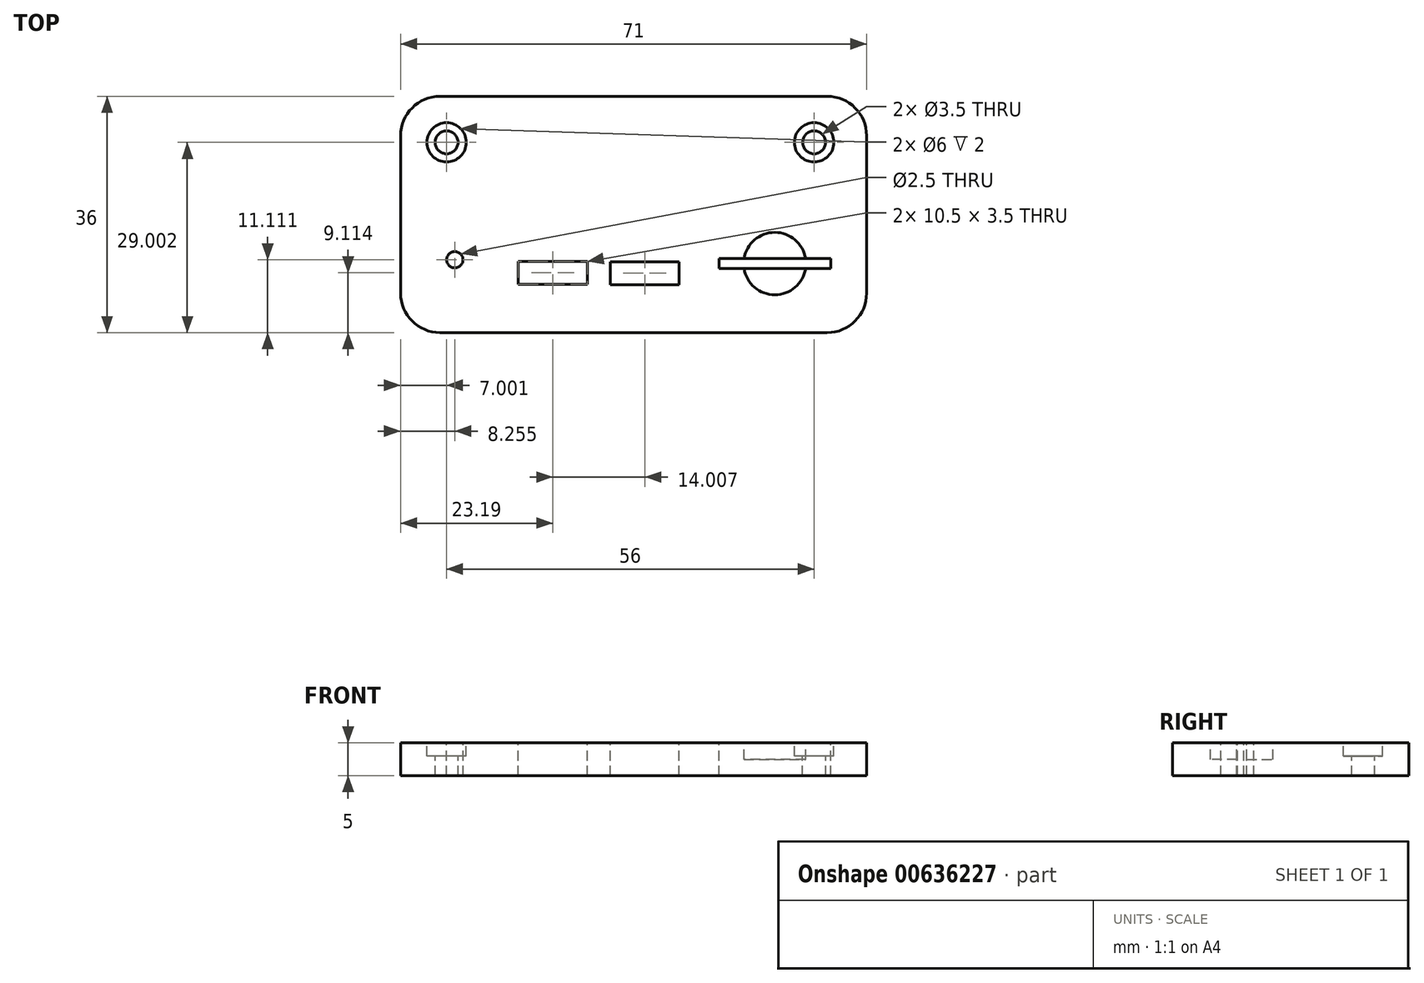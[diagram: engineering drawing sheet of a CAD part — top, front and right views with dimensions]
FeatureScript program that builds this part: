
annotation { "Feature Type Name" : "Feature", "Feature Type Description" : "" }
export const myFeature = defineFeature(function(context is Context, id is Id, definition is map)
    precondition{}
    {
        {
            var Q0;
            Q0=qCreatedBy(makeId("Top.planeOp"),FACE);
            var sketch = newSketch(context, id + "F0", { "sketchPlane" : qUnion([Q0])});
            skCircle(sketch, "E0", {"center": v(27.33, 10.52) * mm, "radius": 1.75 * mm});
            skCircle(sketch, "E1", {"center": v(-28.67, 10.52) * mm, "radius": 1.75 * mm});
            skLineSegment(sketch, "E2", {"start": v(-29.67, 17.52) * mm, "end": v(29.33, 17.52) * mm});
            skArc(sketch, "E3", {"start": v(-29.67, 17.52) * mm, "mid": v(-33.91, 15.77) * mm, "end": v(-35.67, 11.52) * mm});
            skArc(sketch, "E4", {"start": v(35.33, 11.52) * mm, "mid": v(33.57, 15.77) * mm, "end": v(29.33, 17.52) * mm});
            skLineSegment(sketch, "E5", {"start": v(-35.67, 11.52) * mm, "end": v(-35.67, -12.48) * mm});
            skLineSegment(sketch, "E6", {"start": v(-29.67, -18.48) * mm, "end": v(29.33, -18.48) * mm});
            skLineSegment(sketch, "E7", {"start": v(35.33, -12.48) * mm, "end": v(35.33, 11.52) * mm});
            skPoint(sketch, "E8.visualSharp", {"position": v(-35.67, -18.48) * mm});
            skArc(sketch, "E8.filletArc", {"start": v(-35.67, -12.48) * mm, "mid": v(-33.91, -16.72) * mm, "end": v(-29.67, -18.48) * mm});
            skPoint(sketch, "E9.visualSharp", {"position": v(35.33, -18.48) * mm});
            skArc(sketch, "E9.filletArc", {"start": v(29.33, -18.48) * mm, "mid": v(33.57, -16.72) * mm, "end": v(35.33, -12.48) * mm});
            skLineSegment(sketch, "E10.bottom", {"start": v(12.85, -7.2) * mm, "end": v(29.85, -7.2) * mm});
            skLineSegment(sketch, "E10.top", {"start": v(12.85, -8.7) * mm, "end": v(29.85, -8.7) * mm});
            skLineSegment(sketch, "E10.left", {"start": v(12.85, -7.2) * mm, "end": v(12.85, -8.7) * mm});
            skLineSegment(sketch, "E10.right", {"start": v(29.85, -7.2) * mm, "end": v(29.85, -8.7) * mm});
            skCircle(sketch, "E11", {"center": v(21.35, -7.95) * mm, "radius": 4.75 * mm});
            skPoint(sketch, "E11.centerSnap0", {"position": v(29.85, -7.95) * mm});
            skPoint(sketch, "E11.centerSnap1", {"position": v(21.35, -7.2) * mm});
            skLineSegment(sketch, "E12.bottom", {"start": v(-3.72, -7.67) * mm, "end": v(6.78, -7.67) * mm});
            skLineSegment(sketch, "E12.top", {"start": v(-3.72, -11.17) * mm, "end": v(6.78, -11.17) * mm});
            skLineSegment(sketch, "E12.left", {"start": v(-3.72, -7.67) * mm, "end": v(-3.72, -11.17) * mm});
            skLineSegment(sketch, "E12.right", {"start": v(6.78, -7.67) * mm, "end": v(6.78, -11.17) * mm});
            skLineSegment(sketch, "E13.bottom", {"start": v(-17.73, -7.62) * mm, "end": v(-7.23, -7.62) * mm});
            skLineSegment(sketch, "E13.top", {"start": v(-17.73, -11.12) * mm, "end": v(-7.23, -11.12) * mm});
            skLineSegment(sketch, "E13.left", {"start": v(-17.73, -7.62) * mm, "end": v(-17.73, -11.12) * mm});
            skLineSegment(sketch, "E13.right", {"start": v(-7.23, -7.62) * mm, "end": v(-7.23, -11.12) * mm});
            skCircle(sketch, "E14", {"center": v(-27.41, -7.37) * mm, "radius": 1.25 * mm});
            skCircle(sketch, "E15", {"center": v(-28.67, 10.52) * mm, "radius": 3 * mm});
            skCircle(sketch, "E16", {"center": v(27.33, 10.52) * mm, "radius": 3 * mm});
            skLineSegment(sketch, "E17", {"start": v(27.33, 10.52) * mm, "end": v(-28.67, 10.52) * mm});
            skSolve(sketch);
        }
        {
            var Q0;
            Q0=makeQuery(id+"F0.imprint","IMPRINT",FACE,{"disambiguationData":[TD([[makeQuery(id+"F0.imprint","IMPRINT",EDGE,{"derivedFrom":sQuery(id+"F0.wireOp",EDGE,"E2")}),-1.0]])]});
            var Q1;
            Q1=makeQuery(id+"F0.imprint","IMPRINT",FACE,{"disambiguationData":[TD([[makeQuery(id+"F0.imprint","IMPRINT",EDGE,{"derivedFrom":sQuery(id+"F0.wireOp",EDGE,"E1")}),-1.0]])]});
            var Q2;
            {var subQ0=sQuery(id+"F0.wireOp",EDGE,"E11");var subQ1=sQuery(id+"F0.wireOp",EDGE,"E10.top");var subQ2=makeQuery(id+"F0.imprint","INTERSECT",VERTEX,{"disambiguationData":[OD(0.0)],"derivedFrom":[subQ1,subQ0]});Q2=makeQuery(id+"F0.imprint","IMPRINT",FACE,{"disambiguationData":[TD([[makeQuery(id+"F0.imprint","IMPRINT",EDGE,{"disambiguationData":[TD([[subQ2,-1.0]])],"derivedFrom":subQ1}),-1.0]])]});}
            var Q3;
            {var subQ0=sQuery(id+"F0.wireOp",EDGE,"E11");var subQ1=sQuery(id+"F0.wireOp",EDGE,"E10.bottom");var subQ2=makeQuery(id+"F0.imprint","INTERSECT",VERTEX,{"disambiguationData":[OD(0.0)],"derivedFrom":[subQ1,subQ0]});Q3=makeQuery(id+"F0.imprint","IMPRINT",FACE,{"disambiguationData":[TD([[makeQuery(id+"F0.imprint","IMPRINT",EDGE,{"disambiguationData":[TD([[subQ2,-1.0]])],"derivedFrom":subQ1}),1.0]])]});}
            var Q4;
            Q4=makeQuery(id+"F0.imprint","IMPRINT",FACE,{"disambiguationData":[TD([[makeQuery(id+"F0.imprint","IMPRINT",EDGE,{"derivedFrom":sQuery(id+"F0.wireOp",EDGE,"E0")}),-1.0]])]});
            extrude(context, id + "F1", {"entities" : qUnion([Q0, Q1, Q2, Q3, Q4]), "oppositeDirection" : true, "depth" : 5 * mm, "offsetDistance" : 25 * mm});
        }
        {
            var Q0;
            Q0=makeQuery(id+"F0.imprint","IMPRINT",FACE,{"disambiguationData":[TD([[makeQuery(id+"F0.imprint","IMPRINT",EDGE,{"derivedFrom":sQuery(id+"F0.wireOp",EDGE,"E1")}),-1.0]])]});
            var Q1;
            Q1=makeQuery(id+"F0.imprint","IMPRINT",FACE,{"disambiguationData":[TD([[makeQuery(id+"F0.imprint","IMPRINT",EDGE,{"derivedFrom":sQuery(id+"F0.wireOp",EDGE,"E0")}),-1.0]])]});
            extrude(context, id + "F2", {"entities" : qUnion([Q0, Q1]), "operationType" : NewBodyOperationType.REMOVE, "oppositeDirection" : true, "depth" : 2 * mm, "offsetDistance" : 25 * mm});
        }
        {
            var Q0;
            {var subQ0=sQuery(id+"F0.wireOp",EDGE,"E11");var subQ1=sQuery(id+"F0.wireOp",EDGE,"E10.top");var subQ2=makeQuery(id+"F0.imprint","INTERSECT",VERTEX,{"disambiguationData":[OD(0.0)],"derivedFrom":[subQ1,subQ0]});Q0=makeQuery(id+"F0.imprint","IMPRINT",FACE,{"disambiguationData":[TD([[makeQuery(id+"F0.imprint","IMPRINT",EDGE,{"disambiguationData":[TD([[subQ2,-1.0]])],"derivedFrom":subQ1}),-1.0]])]});}
            var Q1;
            {var subQ0=sQuery(id+"F0.wireOp",EDGE,"E11");var subQ1=sQuery(id+"F0.wireOp",EDGE,"E10.bottom");var subQ2=makeQuery(id+"F0.imprint","INTERSECT",VERTEX,{"disambiguationData":[OD(0.0)],"derivedFrom":[subQ1,subQ0]});Q1=makeQuery(id+"F0.imprint","IMPRINT",FACE,{"disambiguationData":[TD([[makeQuery(id+"F0.imprint","IMPRINT",EDGE,{"disambiguationData":[TD([[subQ2,-1.0]])],"derivedFrom":subQ1}),1.0]])]});}
            extrude(context, id + "F3", {"entities" : qUnion([Q0, Q1]), "operationType" : NewBodyOperationType.REMOVE, "oppositeDirection" : true, "depth" : 2.5 * mm, "offsetDistance" : 25 * mm});
        }
    });
